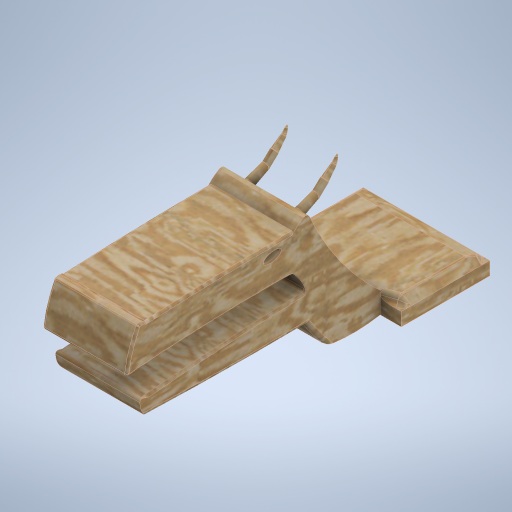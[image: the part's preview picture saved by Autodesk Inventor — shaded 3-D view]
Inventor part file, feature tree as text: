
AUTODESK INVENTOR PART (.ipt)
format: ipt  version: 2024.2 (Build 282272000, 272)  size: 1,772,032 bytes
history: native  units: mm
features: sketch x28, extrude x18, fillet x18, plane x4, chamfer x2, draft x1
ambient origin geometry x8: Origin, YZ Plane, XZ Plane, XY Plane, X Axis, Y Axis, Z Axis, Center Point
bodies: Solid1 (feature_tree)
feature tree (71):
  sketch  "Sketch1"  dims[d0=300.0mm d1=210.0mm]
  sketch  "Sketch2"  dims[d2=300.0mm d3=6.108652mm d4=700.0mm d5=350.0mm]
  sketch  "Sketch3"  dims[d6=7000.0mm]
  extrude  "Extrusion1"  Depth=210.0mm
  extrude  "Extrusion2"  Depth=6.108652mm
  fillet  "Fillet1"  Radius=700.0mm
  fillet  "Fillet2"  Radius=350.0mm
  plane  "Work Plane1"
  chamfer  "Chamfer1"  Distance=50.0mm
  fillet  "Fillet3"  Radius=200.0mm
  chamfer  "Chamfer2"  Distance=18.5mm Angle=45.0deg
  fillet  "Fillet4"  Radius=80.0mm
  fillet  "Fillet5"  Radius=80.0mm
  extrude  "Extrusion3"  Depth=31.5mm TaperAngle=0.0deg
  sketch  "Sketch5"  dims[d8=250.0mm]
  extrude  "Extrusion4"  Depth=5.0mm
  fillet  "Fillet6"  Radius=5.0mm
  fillet  "Fillet7"  Radius=5.0mm
  fillet  "Fillet8"  [1 undecoded]
  extrude  "Extrusion5"  Depth=2.5mm
  extrude  "Extrusion6"  Depth=2.5mm
  fillet  "Fillet9"  Radius=150.0mm
  fillet  "Fillet10"  Radius=31.5mm
  fillet  "Fillet11"  Radius=1000.0mm
  sketch  "Sketch9"  dims[d12=60.0mm]
  extrude  "Extrusion7"  Depth=9.5mm
  extrude  "Extrusion8"  Depth=40.0mm TaperAngle=0.0deg
  extrude  "Extrusion9"  Depth=0.436332mm
  extrude  "Extrusion10"  Depth=3.4mm TaperAngle=0.0deg
  fillet  "Fillet12"  Radius=0.25mm
  plane  "Work Plane2"
  extrude  "Extrusion11"  Depth=30.0mm TaperAngle=0.0deg
  sketch  "Sketch15"  dims[d18=350.0mm]
  extrude  "Extrusion12"  Depth=2.0mm
  fillet  "Fillet13"  Radius=30.0mm
  sketch  "Sketch17"  dims[d20=60.0mm d21=50.0mm d22=0.0mm d23=200.0mm d24=0.0mm]
  draft  "FaceDraft1"
  sketch  "Sketch18"  dims[d25=5.0mm]
  plane  "Work Plane3"
  extrude  "Extrusion13"  Depth=2.0mm
  fillet  "Fillet14"  Radius=3.490659mm
  extrude  "Extrusion14"  Depth=5.0mm TaperAngle=0.0deg
  fillet  "Fillet15"  Radius=2.0mm
  extrude  "Extrusion15"  Depth=10.0mm
  fillet  "Fillet16"  Radius=5.0mm
  sketch  "Sketch22"  dims[d38=31.5mm d39=31.5mm d40=-0.872665mm d41=-0.872665mm d42=5.0mm d43=5.0mm d44=5.0mm d45=0.0mm d46=0.0mm]
  sketch  "Sketch23"  dims[d47=150.0mm d48=0.0mm d49=2.5mm]
  sketch  "Sketch24"  dims[d50=2.5mm d51=2.5mm d52=150.0mm d53=0.0mm d54=31.5mm d55=0.0mm d56=1000.0mm d57=0.0mm]
  plane  "Work Plane4"
  extrude  "Extrusion16"  Depth=0.99mm
  fillet  "Fillet17"  [1 undecoded]
  extrude  "Extrusion17"  TaperAngle=0.0deg  [1 undecoded]
  sketch  "Sketch27"  dims[d65=5.25mm d66=0.436332mm]
  extrude  "Extrusion18"  TaperAngle=0.0deg  [1 undecoded]
  fillet  "Fillet18"  [1 undecoded]
  sketch  "Sketch4"  dims[d7=25.0mm]
  sketch  "Sketch6"  dims[d9=40.0mm]
  sketch  "Sketch7"  dims[d10=15.358897mm]
  sketch  "Sketch8"  dims[d11=4000.0mm]
  sketch  "Sketch10"  dims[d13=125.0mm]
  sketch  "Sketch11"  dims[d14=5000.0mm]
  sketch  "Sketch12"  dims[d15=50.0mm]
  sketch  "Sketch13"  dims[d16=6200.0mm]
  sketch  "Sketch14"  dims[d17=625.0mm]
  sketch  "Sketch16"  dims[d19=49.866924mm]
  sketch  "Sketch19"  dims[d26=10.0mm d27=18.5mm d28=125.0mm d29=45.0deg d30=80.0mm]
  sketch  "Sketch20"  dims[d31=18.5mm d32=125.0mm d33=45.0deg d34=80.0mm]
  sketch  "Sketch21"  dims[d35=50.0mm d36=31.5mm d37=0.0mm]
  sketch  "Sketch25"  dims[d58=31.5mm d59=0.0mm d60=9.5mm]
  sketch  "Sketch26"  dims[d61=10.0mm d62=0.0mm d63=40.0mm d64=0.0mm]
  sketch  "Sketch28"  dims[d67=-3.490659mm d68=3.4mm d69=0.0mm d70=0.25mm d71=30.0mm d72=0.0mm d73=2.0mm d74=30.0mm d75=-0.872665mm d76=2.0mm d77=3.490659mm d78=5.0mm d79=3.0mm d80=0.0mm d81=0.0mm d82=2.0mm d83=10.0mm d84=-1.745329mm d85=5.0mm d86=-1.745329mm d87=0.99mm d88=0.0mm d89=0.0mm d90=0.0mm]
note: 5 required parameter values undecoded (feature->parameter linkage not recoverable at this tier; creation-order binding heuristic only, values carry confidence <= 0.55)
